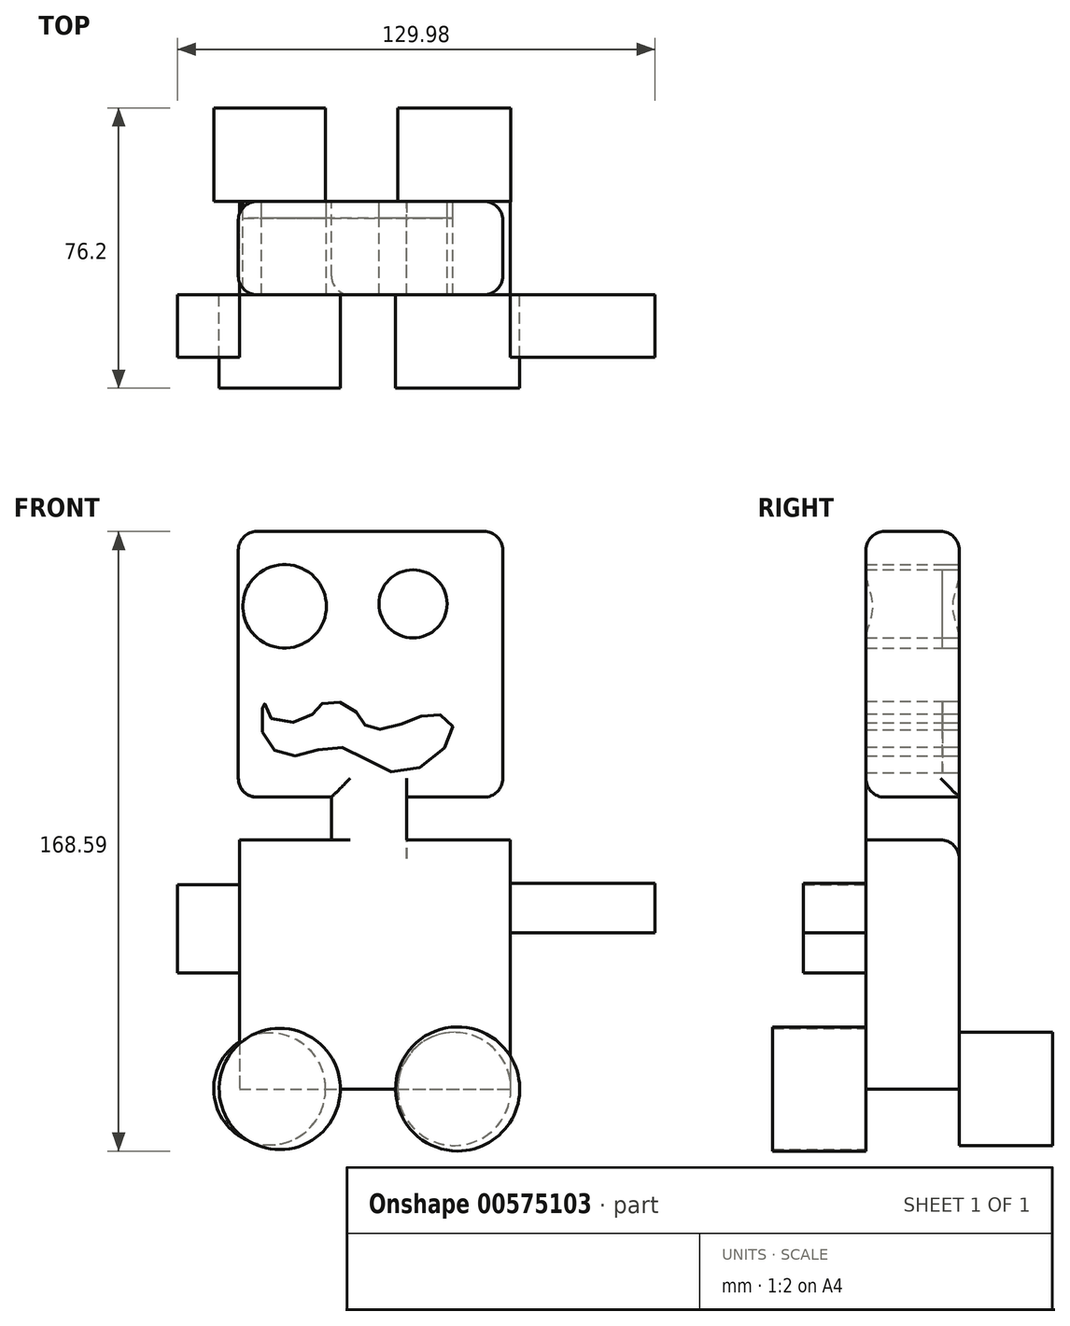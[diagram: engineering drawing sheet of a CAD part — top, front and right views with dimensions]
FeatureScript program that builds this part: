
annotation { "Feature Type Name" : "Feature", "Feature Type Description" : "" }
export const myFeature = defineFeature(function(context is Context, id is Id, definition is map)
    precondition{}
    {
        {
            var Q0;
            Q0=qCreatedBy(makeId("Front.planeOp"),FACE);
            var sketch = newSketch(context, id + "F0", { "sketchPlane" : qUnion([Q0])});
            skLineSegment(sketch, "E0.bottom", {"start": v(-76.65, 76.33) * mm, "end": v(-4.72, 76.33) * mm});
            skLineSegment(sketch, "E0.top", {"start": v(-76.65, 4.04) * mm, "end": v(-4.72, 4.04) * mm});
            skLineSegment(sketch, "E0.left", {"start": v(-76.65, 76.33) * mm, "end": v(-76.65, 4.04) * mm});
            skLineSegment(sketch, "E0.right", {"start": v(-4.72, 76.33) * mm, "end": v(-4.72, 4.04) * mm});
            skCircle(sketch, "E1", {"center": v(-64.06, 55.96) * mm, "radius": 11.35 * mm});
            skCircle(sketch, "E2", {"center": v(-29.1, 56.64) * mm, "radius": 9.26 * mm});
            skFitSpline(sketch, "E3", {"points": [v(-70.06, 21.74) * mm, v(-62.26, 15.27) * mm, v(-48.76, 17.58) * mm, v(-32.15, 10.72) * mm, v(-18.25, 22.36) * mm, v(-23.2, 26.69) * mm, v(-33.39, 23.5) * mm, v(-41.68, 23.16) * mm, v(-45.38, 28.04) * mm, v(-53.5, 29.72) * mm, v(-57.38, 25.79) * mm, v(-68.2, 25.85) * mm, v(-69.62, 30.07) * mm, v(-70.06, 21.74) * mm]});
            skSolve(sketch);
        }
        {
            var Q0;
            Q0=makeQuery(id+"F0.imprint","IMPRINT",FACE,{"disambiguationData":[TD([[makeQuery(id+"F0.imprint","IMPRINT",EDGE,{"derivedFrom":sQuery(id+"F0.wireOp",EDGE,"E0.bottom")}),-1.0]])]});
            var sketch = newSketch(context, id + "F1", { "sketchPlane" : qUnion([Q0])});
            skSolve(sketch);
        }
        {
            var Q0;
            Q0 = qSketchRegion(id + "F1", true);
            var Q1;
            Q1=makeQuery(id+"F0.imprint","IMPRINT",FACE,{"disambiguationData":[TD([[makeQuery(id+"F0.imprint","IMPRINT",EDGE,{"derivedFrom":sQuery(id+"F0.wireOp",EDGE,"E3")}),1.0]])]});
            var Q2;
            Q2=makeQuery(id+"F0.imprint","IMPRINT",FACE,{"disambiguationData":[TD([[makeQuery(id+"F0.imprint","IMPRINT",EDGE,{"derivedFrom":sQuery(id+"F0.wireOp",EDGE,"E2")}),1.0]])]});
            var Q3;
            Q3=makeQuery(id+"F0.imprint","IMPRINT",FACE,{"disambiguationData":[TD([[makeQuery(id+"F0.imprint","IMPRINT",EDGE,{"derivedFrom":sQuery(id+"F0.wireOp",EDGE,"E1")}),1.0]])]});
            extrude(context, id + "F2", {"entities" : qUnion([Q0, Q1, Q2, Q3]), "depth" : 4.57 * mm, "offsetDistance" : 25.4 * mm});
        }
        {
            var Q0;
            Q0=makeQuery(id+"F1.imprint","IMPRINT",FACE,{"disambiguationData":[TD([[makeQuery(id+"F1.imprint","IMPRINT",EDGE,{"derivedFrom":makeQuery(id+"F0.imprint","IMPRINT",EDGE,{"derivedFrom":sQuery(id+"F0.wireOp",EDGE,"E0.bottom")})}),-1.0]])]});
            extrude(context, id + "F3", {"entities" : qUnion([Q0]), "depth" : 25.4 * mm, "offsetDistance" : 25.4 * mm});
        }
        {
            var Q0;
            Q0=qCreatedBy(makeId("Front.planeOp"),FACE);
            var sketch = newSketch(context, id + "F4", { "sketchPlane" : qUnion([Q0])});
            skLineSegment(sketch, "E4.bottom", {"start": v(-51.32, 4.94) * mm, "end": v(-30.84, 4.94) * mm});
            skLineSegment(sketch, "E4.top", {"start": v(-51.32, -7.62) * mm, "end": v(-30.84, -7.62) * mm});
            skLineSegment(sketch, "E4.left", {"start": v(-51.32, 4.94) * mm, "end": v(-51.32, -7.62) * mm});
            skLineSegment(sketch, "E4.right", {"start": v(-30.84, 4.94) * mm, "end": v(-30.84, -7.62) * mm});
            skLineSegment(sketch, "E5.bottom", {"start": v(-76.3, -7.62) * mm, "end": v(-2.7, -7.62) * mm});
            skLineSegment(sketch, "E5.top", {"start": v(-76.3, -75.37) * mm, "end": v(-2.7, -75.37) * mm});
            skLineSegment(sketch, "E5.left", {"start": v(-76.3, -7.62) * mm, "end": v(-76.3, -75.37) * mm});
            skLineSegment(sketch, "E5.right", {"start": v(-2.7, -7.62) * mm, "end": v(-2.7, -75.37) * mm});
            skSolve(sketch);
        }
        {
            var Q0;
            Q0 = qSketchRegion(id + "F4", true);
            extrude(context, id + "F5", {"entities" : qUnion([Q0]), "operationType" : NewBodyOperationType.ADD, "depth" : 25.4 * mm, "offsetDistance" : 25.4 * mm});
        }
        {
            var Q0;
            Q0=makeQuery(id+"F5.boolean.opBoolean","MERGE",FACE,{"derivedFrom":[makeQuery(id+"F3.opExtrude","CAP_FACE",FACE,{"disambiguationData":[OSD([sQuery(id+"F0.wireOp",EDGE,"E0.bottom"),sQuery(id+"F0.wireOp",EDGE,"E0.top"),sQuery(id+"F0.wireOp",EDGE,"E0.left"),sQuery(id+"F0.wireOp",EDGE,"E0.right"),sQuery(id+"F0.wireOp",EDGE,"E1"),sQuery(id+"F0.wireOp",EDGE,"E2"),sQuery(id+"F0.wireOp",EDGE,"E3")])],"isStart":false}),makeQuery(id+"F5.opExtrude","CAP_FACE",FACE,{"disambiguationData":[OSD([sQuery(id+"F4.wireOp",EDGE,"E4.bottom"),sQuery(id+"F4.wireOp",EDGE,"E4.left"),sQuery(id+"F4.wireOp",EDGE,"E4.right"),sQuery(id+"F4.wireOp",EDGE,"E5.bottom"),sQuery(id+"F4.wireOp",EDGE,"E5.top"),sQuery(id+"F4.wireOp",EDGE,"E5.left"),sQuery(id+"F4.wireOp",EDGE,"E5.right")])],"isStart":false})]});
            var sketch = newSketch(context, id + "F6", { "sketchPlane" : qUnion([Q0])});
            skLineSegment(sketch, "E6.bottom", {"start": v(-2.7, -19.44) * mm, "end": v(36.73, -19.44) * mm});
            skLineSegment(sketch, "E6.top", {"start": v(-2.7, -32.94) * mm, "end": v(36.73, -32.94) * mm});
            skLineSegment(sketch, "E6.left", {"start": v(-2.7, -19.44) * mm, "end": v(-2.7, -32.94) * mm});
            skLineSegment(sketch, "E6.right", {"start": v(36.73, -19.44) * mm, "end": v(36.73, -32.94) * mm});
            skLineSegment(sketch, "E7.bottom", {"start": v(-76.3, -19.78) * mm, "end": v(-93.25, -19.78) * mm});
            skLineSegment(sketch, "E7.top", {"start": v(-76.3, -43.82) * mm, "end": v(-93.25, -43.82) * mm});
            skLineSegment(sketch, "E7.left", {"start": v(-76.3, -19.78) * mm, "end": v(-76.3, -43.82) * mm});
            skLineSegment(sketch, "E7.right", {"start": v(-93.25, -19.78) * mm, "end": v(-93.25, -43.82) * mm});
            skSolve(sketch);
        }
        {
            var Q0;
            Q0 = qSketchRegion(id + "F6", true);
            extrude(context, id + "F7", {"entities" : qUnion([Q0]), "depth" : 17.02 * mm, "offsetDistance" : 25.4 * mm});
        }
        {
            var Q0;
            Q0=makeQuery(id+"F5.boolean.opBoolean","MERGE",FACE,{"derivedFrom":[makeQuery(id+"F3.opExtrude","CAP_FACE",FACE,{"disambiguationData":[OSD([sQuery(id+"F0.wireOp",EDGE,"E0.bottom"),sQuery(id+"F0.wireOp",EDGE,"E0.top"),sQuery(id+"F0.wireOp",EDGE,"E0.left"),sQuery(id+"F0.wireOp",EDGE,"E0.right"),sQuery(id+"F0.wireOp",EDGE,"E1"),sQuery(id+"F0.wireOp",EDGE,"E2"),sQuery(id+"F0.wireOp",EDGE,"E3")])],"isStart":false}),makeQuery(id+"F5.opExtrude","CAP_FACE",FACE,{"disambiguationData":[OSD([sQuery(id+"F4.wireOp",EDGE,"E4.bottom"),sQuery(id+"F4.wireOp",EDGE,"E4.left"),sQuery(id+"F4.wireOp",EDGE,"E4.right"),sQuery(id+"F4.wireOp",EDGE,"E5.bottom"),sQuery(id+"F4.wireOp",EDGE,"E5.top"),sQuery(id+"F4.wireOp",EDGE,"E5.left"),sQuery(id+"F4.wireOp",EDGE,"E5.right")])],"isStart":false})]});
            var sketch = newSketch(context, id + "F8", { "sketchPlane" : qUnion([Q0])});
            skCircle(sketch, "E8", {"center": v(-65.39, -75.37) * mm, "radius": 16.48 * mm});
            skCircle(sketch, "E9", {"center": v(-16.99, -75.37) * mm, "radius": 16.89 * mm});
            skSolve(sketch);
        }
        {
            var Q0;
            Q0 = qSketchRegion(id + "F8", true);
            extrude(context, id + "F9", {"entities" : qUnion([Q0]), "operationType" : NewBodyOperationType.ADD, "depth" : 25.4 * mm, "offsetDistance" : 25.4 * mm});
        }
        {
            var Q0;
            Q0=makeQuery(id+"F5.boolean.opBoolean","MERGE",FACE,{"derivedFrom":[makeQuery(id+"F3.opExtrude","CAP_FACE",FACE,{"disambiguationData":[OSD([sQuery(id+"F0.wireOp",EDGE,"E0.bottom"),sQuery(id+"F0.wireOp",EDGE,"E0.top"),sQuery(id+"F0.wireOp",EDGE,"E0.left"),sQuery(id+"F0.wireOp",EDGE,"E0.right"),sQuery(id+"F0.wireOp",EDGE,"E1"),sQuery(id+"F0.wireOp",EDGE,"E2"),sQuery(id+"F0.wireOp",EDGE,"E3")])],"isStart":true}),makeQuery(id+"F5.opExtrude","CAP_FACE",FACE,{"disambiguationData":[OSD([sQuery(id+"F4.wireOp",EDGE,"E4.bottom"),sQuery(id+"F4.wireOp",EDGE,"E4.left"),sQuery(id+"F4.wireOp",EDGE,"E4.right"),sQuery(id+"F4.wireOp",EDGE,"E5.bottom"),sQuery(id+"F4.wireOp",EDGE,"E5.top"),sQuery(id+"F4.wireOp",EDGE,"E5.left"),sQuery(id+"F4.wireOp",EDGE,"E5.right")])],"isStart":true})]});
            var sketch = newSketch(context, id + "F10", { "sketchPlane" : qUnion([Q0])});
            skCircle(sketch, "E10", {"center": v(17.89, -75.37) * mm, "radius": 15.4 * mm});
            skCircle(sketch, "E11", {"center": v(68.13, -75.37) * mm, "radius": 15.23 * mm});
            skSolve(sketch);
        }
        {
            var Q0;
            Q0 = qSketchRegion(id + "F10", true);
            extrude(context, id + "F11", {"entities" : qUnion([Q0]), "operationType" : NewBodyOperationType.ADD, "depth" : 25.4 * mm, "offsetDistance" : 25.4 * mm});
        }
        {
            var Q0;
            Q0=makeQuery(id+"F3.opExtrude","CAP_EDGE",EDGE,{"disambiguationData":[OSD([sQuery(id+"F0.wireOp",EDGE,"E0.bottom")])],"isStart":false});
            var Q1;
            Q1=makeQuery(id+"F3.opExtrude","SWEPT_EDGE",EDGE,{"disambiguationData":[OSD([sQuery(id+"F0.wireOp",EDGE,"E0.bottom"),sQuery(id+"F0.wireOp",EDGE,"E0.left")])]});
            var Q2;
            Q2=makeQuery(id+"F3.opExtrude","SWEPT_EDGE",EDGE,{"disambiguationData":[OSD([sQuery(id+"F0.wireOp",EDGE,"E0.bottom"),sQuery(id+"F0.wireOp",EDGE,"E0.right")])]});
            var Q3;
            Q3=makeQuery(id+"F3.opExtrude","SWEPT_FACE",FACE,{"disambiguationData":[OSD([sQuery(id+"F0.wireOp",EDGE,"E0.bottom")])]});
            var Q4;
            Q4=makeQuery(id+"F3.opExtrude","CAP_EDGE",EDGE,{"disambiguationData":[OSD([sQuery(id+"F0.wireOp",EDGE,"E0.right")])],"isStart":false});
            var Q5;
            Q5=makeQuery(id+"F3.opExtrude","SWEPT_EDGE",EDGE,{"disambiguationData":[OSD([sQuery(id+"F0.wireOp",EDGE,"E0.top"),sQuery(id+"F0.wireOp",EDGE,"E0.right")])]});
            var Q6;
            Q6=makeQuery(id+"F3.opExtrude","CAP_EDGE",EDGE,{"disambiguationData":[OSD([sQuery(id+"F0.wireOp",EDGE,"E0.right")])],"isStart":true});
            var Q7;
            Q7=makeQuery(id+"F3.opExtrude","CAP_EDGE",EDGE,{"disambiguationData":[OSD([sQuery(id+"F0.wireOp",EDGE,"E0.left")])],"isStart":false});
            var Q8;
            Q8=makeQuery(id+"F3.opExtrude","CAP_EDGE",EDGE,{"disambiguationData":[OSD([sQuery(id+"F0.wireOp",EDGE,"E0.left")])],"isStart":true});
            var Q9;
            Q9=makeQuery(id+"F3.opExtrude","SWEPT_EDGE",EDGE,{"disambiguationData":[OSD([sQuery(id+"F0.wireOp",EDGE,"E0.top"),sQuery(id+"F0.wireOp",EDGE,"E0.left")])]});
            var Q10;
            {var subQ1=sQuery(id+"F0.wireOp",EDGE,"E0.top");var subQ2=sQuery(id+"F0.wireOp",EDGE,"E0.left");Q10=makeQuery(id+"F5.boolean.opBoolean","SPLIT",EDGE,{"disambiguationData":[TD([makeQuery(id+"F3.opExtrude","SWEPT_FACE",FACE,{"disambiguationData":[OSD([subQ2])]})])],"derivedFrom":makeQuery(id+"F3.opExtrude","CAP_EDGE",EDGE,{"disambiguationData":[OSD([subQ1])],"isStart":false})});}
            var Q11;
            {var subQ1=sQuery(id+"F0.wireOp",EDGE,"E0.top");var subQ2=sQuery(id+"F0.wireOp",EDGE,"E0.right");Q11=makeQuery(id+"F5.boolean.opBoolean","SPLIT",EDGE,{"disambiguationData":[TD([makeQuery(id+"F3.opExtrude","SWEPT_FACE",FACE,{"disambiguationData":[OSD([subQ2])]})])],"derivedFrom":makeQuery(id+"F3.opExtrude","CAP_EDGE",EDGE,{"disambiguationData":[OSD([subQ1])],"isStart":false})});}
            var Q12;
            Q12=makeQuery(id+"F5.opExtrude","CAP_EDGE",EDGE,{"disambiguationData":[OSD([sQuery(id+"F4.wireOp",EDGE,"E4.left")])],"isStart":false});
            var Q13;
            {var subQ0=sQuery(id+"F4.wireOp",EDGE,"E5.bottom");Q13=makeQuery(id+"F5.opExtrude","CAP_EDGE",EDGE,{"disambiguationData":[OSD([subQ0]),TDD([makeQuery(id+"F4.imprint","IMPRINT",EDGE,{"disambiguationData":[TD([[makeQuery(id+"F4.imprint","INTERSECT",VERTEX,{"derivedFrom":[sQuery(id+"F4.wireOp",EDGE,"E4.right"),subQ0]}),-1.0]])],"derivedFrom":subQ0})])],"isStart":true});}
            fillet(context, id + "F12", {"entities" : qUnion([Q0, Q1, Q2, Q3, Q4, Q5, Q6, Q7, Q8, Q9, Q10, Q11, Q12, Q13]), "radius" : 5.08 * mm, "tangentPropagation" : true, "allowEdgeOverflow" : false});
        }
    });
